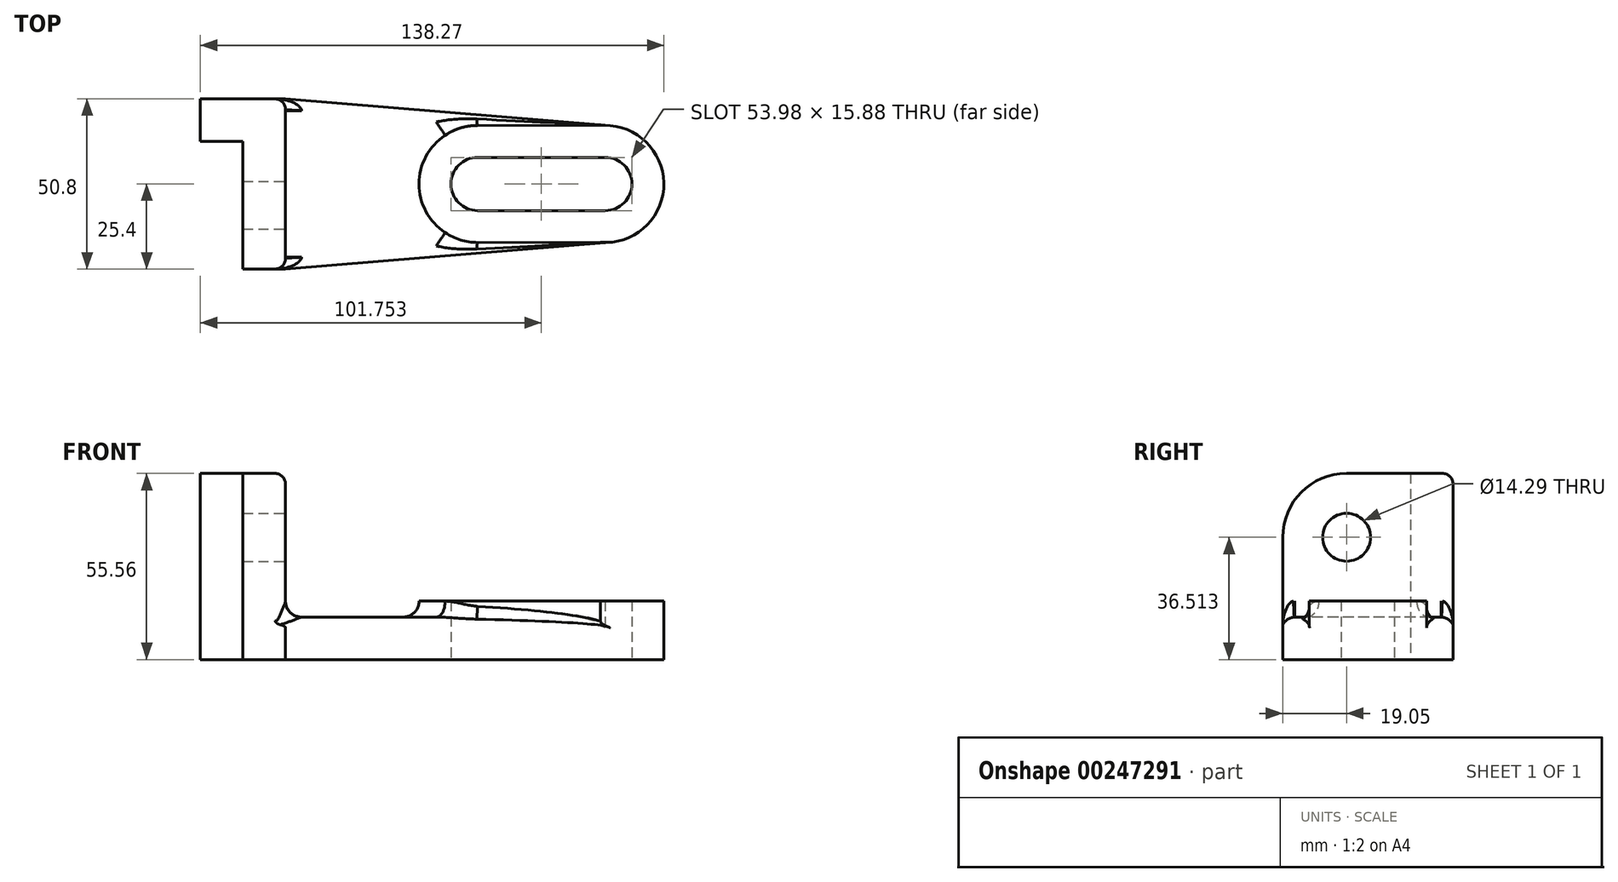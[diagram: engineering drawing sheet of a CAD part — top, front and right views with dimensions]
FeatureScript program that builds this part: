
annotation { "Feature Type Name" : "Feature", "Feature Type Description" : "" }
export const myFeature = defineFeature(function(context is Context, id is Id, definition is map)
    precondition{}
    {
        {
            var Q0;
            Q0=qCreatedBy(makeId("Top.planeOp"),FACE);
            var sketch = newSketch(context, id + "F0", { "sketchPlane" : qUnion([Q0])});
            skLineSegment(sketch, "E0.bottom", {"start": v(-109.54, 25.4) * mm, "end": v(-96.84, 25.4) * mm});
            skLineSegment(sketch, "E0.top", {"start": v(-109.54, -25.4) * mm, "end": v(-96.84, -25.4) * mm});
            skLineSegment(sketch, "E0.left", {"start": v(-109.54, 12.7) * mm, "end": v(-109.54, -25.4) * mm});
            skLineSegment(sketch, "E0.right", {"start": v(-96.84, 25.4) * mm, "end": v(-96.84, -25.4) * mm});
            skLineSegment(sketch, "E1", {"start": v(-109.54, 25.4) * mm, "end": v(-122.24, 25.4) * mm});
            skLineSegment(sketch, "E2", {"start": v(-122.24, 25.4) * mm, "end": v(-122.24, 12.7) * mm});
            skLineSegment(sketch, "E3", {"start": v(-122.24, 12.7) * mm, "end": v(-109.54, 12.7) * mm});
            skLineSegment(sketch, "E4", {"start": v(-96.84, 25.4) * mm, "end": v(0, 17.4) * mm});
            skLineSegment(sketch, "E5", {"start": v(-96.84, -25.4) * mm, "end": v(0, -17.4) * mm});
            skPoint(sketch, "E6", {"position": v(0, 0) * mm});
            skLineSegment(sketch, "E7", {"start": v(-0.02, 17.34) * mm, "end": v(-0.02, 17.34) * mm});
            skLineSegment(sketch, "E8", {"start": v(-0.17, -17.34) * mm, "end": v(-0.17, -17.34) * mm});
            skArc(sketch, "E9", {"start": v(0, -17.4) * mm, "mid": v(16.03, 0) * mm, "end": v(0, 17.4) * mm});
            skSolve(sketch);
        }
        {
            var Q0;
            Q0=makeQuery(id+"F0.imprint","IMPRINT",FACE,{"disambiguationData":[TD([[makeQuery(id+"F0.imprint","IMPRINT",EDGE,{"derivedFrom":sQuery(id+"F0.wireOp",EDGE,"E0.bottom")}),-1.0]])]});
            extrude(context, id + "F1", {"entities" : qUnion([Q0]), "depth" : 55.56 * mm});
        }
        {
            var Q0;
            Q0=makeQuery(id+"F1.opExtrude","CAP_EDGE",EDGE,{"disambiguationData":[OSD([sQuery(id+"F0.wireOp",EDGE,"E0.right")])],"isStart":false});
            var Q1;
            Q1=makeQuery(id+"FIujw7qw0SntBFI_1.boolean.opBoolean","SPLIT",EDGE,{"derivedFrom":makeQuery(id+"F1.opExtrude","SWEPT_EDGE",EDGE,{"disambiguationData":[OSD([sQuery(id+"F0.wireOp",EDGE,"E0.top"),sQuery(id+"F0.wireOp",EDGE,"E0.right"),sQuery(id+"F0.wireOp",EDGE,"E5")])]})});
            var Q2;
            Q2=makeQuery(id+"FIujw7qw0SntBFI_1.boolean.opBoolean","SPLIT",EDGE,{"derivedFrom":makeQuery(id+"F1.opExtrude","SWEPT_EDGE",EDGE,{"disambiguationData":[OSD([sQuery(id+"F0.wireOp",EDGE,"E0.bottom"),sQuery(id+"F0.wireOp",EDGE,"E0.right"),sQuery(id+"F0.wireOp",EDGE,"E4")])]})});
            var Q3;
            Q3=makeQuery(id+"F1.opExtrude","CAP_EDGE",EDGE,{"disambiguationData":[OSD([sQuery(id+"F0.wireOp",EDGE,"E0.bottom"),sQuery(id+"F0.wireOp",EDGE,"E1")])],"isStart":false});
            fillet(context, id + "F2", {"entities" : qUnion([Q0, Q1, Q2, Q3]), "radius" : 3.17 * mm, "tangentPropagation" : true, "allowEdgeOverflow" : false});
        }
        {
            var Q0;
            Q0=makeQuery(id+"F1.opExtrude","CAP_EDGE",EDGE,{"disambiguationData":[OSD([sQuery(id+"F0.wireOp",EDGE,"E0.top")])],"isStart":false});
            fillet(context, id + "F3", {"entities" : qUnion([Q0]), "radius" : 19.05 * mm, "tangentPropagation" : true, "allowEdgeOverflow" : false});
        }
        {
            var Q0;
            Q0 = qSketchRegion(id + "F0", true);
            extrude(context, id + "F4", {"entities" : qUnion([Q0]), "operationType" : NewBodyOperationType.ADD, "depth" : 12.7 * mm});
        }
        {
            var Q0;
            Q0=makeQuery(id+"F4.opExtrude","CAP_FACE",FACE,{"disambiguationData":[OSD([sQuery(id+"F0.wireOp",EDGE,"E0.bottom"),sQuery(id+"F0.wireOp",EDGE,"E0.top"),sQuery(id+"F0.wireOp",EDGE,"E0.left"),sQuery(id+"F0.wireOp",EDGE,"E1"),sQuery(id+"F0.wireOp",EDGE,"E2"),sQuery(id+"F0.wireOp",EDGE,"E3"),sQuery(id+"F0.wireOp",EDGE,"E4"),sQuery(id+"F0.wireOp",EDGE,"E5"),sQuery(id+"F0.wireOp",EDGE,"E9")])],"isStart":false});
            var sketch = newSketch(context, id + "F5", { "sketchPlane" : qUnion([Q0])});
            skArc(sketch, "E10", {"start": v(-2.85, -17.4) * mm, "mid": v(16.01, -0.7) * mm, "end": v(-1.44, 17.46) * mm});
            skArc(sketch, "E11", {"start": v(-1.44, -7.94) * mm, "mid": v(6.5, 0) * mm, "end": v(-1.44, 7.94) * mm});
            skArc(sketch, "E12", {"start": v(-39.54, 17.46) * mm, "mid": v(-57, -0.03) * mm, "end": v(-39.48, -17.46) * mm});
            skArc(sketch, "E13", {"start": v(-39.54, 7.94) * mm, "mid": v(-47.47, 0) * mm, "end": v(-39.54, -7.94) * mm});
            skLineSegment(sketch, "E14", {"start": v(-39.54, 7.94) * mm, "end": v(-1.44, 7.94) * mm});
            skLineSegment(sketch, "E15", {"start": v(-39.54, -7.94) * mm, "end": v(-1.44, -7.94) * mm});
            skLineSegment(sketch, "E16", {"start": v(-1.44, 17.46) * mm, "end": v(-1.44, 17.52) * mm, "construction": true});
            skLineSegment(sketch, "E17", {"start": v(-1.44, 17.52) * mm, "end": v(-1.44, 17.46) * mm, "construction": true});
            skLineSegment(sketch, "E18", {"start": v(-39.54, 17.46) * mm, "end": v(-1.44, 17.52) * mm});
            skLineSegment(sketch, "E19", {"start": v(-39.54, -17.46) * mm, "end": v(-1.44, -17.4) * mm});
            skSolve(sketch);
        }
        {
            var Q0;
            Q0=makeQuery(id+"F5.imprint","IMPRINT",FACE,{"disambiguationData":[TD([[makeQuery(id+"F5.imprint","IMPRINT",EDGE,{"derivedFrom":sQuery(id+"F5.wireOp",EDGE,"E11")}),-1.0]])]});
            extrude(context, id + "F6", {"entities" : qUnion([Q0]), "operationType" : NewBodyOperationType.ADD, "depth" : 4.76 * mm});
        }
        {
            var Q0;
            Q0=makeQuery(id+"F4.opExtrude","CAP_EDGE",EDGE,{"disambiguationData":[OSD([sQuery(id+"F0.wireOp",EDGE,"E5")])],"isStart":false});
            var Q1;
            Q1=makeQuery(id+"F4.opExtrude","CAP_EDGE",EDGE,{"disambiguationData":[OSD([sQuery(id+"F0.wireOp",EDGE,"E4")])],"isStart":false});
            fillet(context, id + "F7", {"entities" : qUnion([Q0, Q1]), "radius" : 3.17 * mm, "tangentPropagation" : true, "allowEdgeOverflow" : false});
        }
        {
            var Q0;
            Q0=makeQuery(id+"F6.opExtrude","CAP_EDGE",EDGE,{"disambiguationData":[OSD([sQuery(id+"F5.wireOp",EDGE,"E12")])],"isStart":true});
            var Q1;
            Q1=makeQuery(id+"F7.opFillet","BLEND_EDGE",EDGE,{"blendedFrom":[makeQuery(id+"F4.opExtrude","CAP_EDGE",EDGE,{"disambiguationData":[OSD([sQuery(id+"F0.wireOp",EDGE,"E5")])],"isStart":false}),makeQuery(id+"F6.opExtrude","SWEPT_FACE",FACE,{"disambiguationData":[OSD([sQuery(id+"F5.wireOp",EDGE,"E19")])]})],"blendedInto":[makeQuery(id+"F6.opExtrude","SWEPT_FACE",FACE,{"disambiguationData":[OSD([sQuery(id+"F5.wireOp",EDGE,"E19")])]})]});
            var Q2;
            Q2=makeQuery(id+"F7.opFillet","BLEND_EDGE",EDGE,{"blendedFrom":[makeQuery(id+"F4.opExtrude","CAP_EDGE",EDGE,{"disambiguationData":[OSD([sQuery(id+"F0.wireOp",EDGE,"E4")])],"isStart":false}),makeQuery(id+"F6.opExtrude","SWEPT_FACE",FACE,{"disambiguationData":[OSD([sQuery(id+"F5.wireOp",EDGE,"E18")])]})],"blendedInto":[makeQuery(id+"F6.opExtrude","SWEPT_FACE",FACE,{"disambiguationData":[OSD([sQuery(id+"F5.wireOp",EDGE,"E18")])]})]});
            fillet(context, id + "F8", {"entities" : qUnion([Q0, Q1, Q2]), "radius" : 4.76 * mm, "tangentPropagation" : true, "allowEdgeOverflow" : false});
        }
        {
            var Q0;
            Q0=makeQuery(id+"F6.boolean.opBoolean","SPLIT",FACE,{"disambiguationData":[TD([makeQuery(id+"F6.opExtrude","SWEPT_FACE",FACE,{"disambiguationData":[OSD([sQuery(id+"F5.wireOp",EDGE,"E11")])]})])],"derivedFrom":makeQuery(id+"F4.opExtrude","CAP_FACE",FACE,{"disambiguationData":[OSD([sQuery(id+"F0.wireOp",EDGE,"E0.bottom"),sQuery(id+"F0.wireOp",EDGE,"E0.top"),sQuery(id+"F0.wireOp",EDGE,"E0.left"),sQuery(id+"F0.wireOp",EDGE,"E1"),sQuery(id+"F0.wireOp",EDGE,"E2"),sQuery(id+"F0.wireOp",EDGE,"E3"),sQuery(id+"F0.wireOp",EDGE,"E4"),sQuery(id+"F0.wireOp",EDGE,"E5"),sQuery(id+"F0.wireOp",EDGE,"E9")])],"isStart":false})});
            extrude(context, id + "F9", {"entities" : qUnion([Q0]), "operationType" : NewBodyOperationType.REMOVE, "endBound" : BoundingType.THROUGH_ALL, "oppositeDirection" : true, "depth" : 25.4 * mm});
        }
        {
            var Q0;
            Q0=makeQuery(id+"F1.opExtrude","SWEPT_FACE",FACE,{"disambiguationData":[OSD([sQuery(id+"F0.wireOp",EDGE,"E0.right")])]});
            var sketch = newSketch(context, id + "F10", { "sketchPlane" : qUnion([Q0])});
            skLineSegment(sketch, "E20", {"start": v(-6.35, 36.51) * mm, "end": v(-22.22, 36.51) * mm, "construction": true});
            skLineSegment(sketch, "E21", {"start": v(-6.35, 52.39) * mm, "end": v(-6.35, 36.51) * mm, "construction": true});
            skCircle(sketch, "E22", {"center": v(-6.35, 36.51) * mm, "radius": 7.14 * mm});
            skSolve(sketch);
        }
        {
            var Q0;
            Q0=makeQuery(id+"F10.imprint","IMPRINT",FACE,{"disambiguationData":[TD([[makeQuery(id+"F10.imprint","IMPRINT",EDGE,{"derivedFrom":sQuery(id+"F10.wireOp",EDGE,"E22")}),1.0]])]});
            extrude(context, id + "F11", {"entities" : qUnion([Q0]), "operationType" : NewBodyOperationType.REMOVE, "endBound" : BoundingType.THROUGH_ALL, "oppositeDirection" : true, "depth" : 25.4 * mm});
        }
        {
            var Q0;
            Q0=makeQuery(id+"F4.boolean.opBoolean","INTERSECT",EDGE,{"derivedFrom":[makeQuery(id+"F1.opExtrude","SWEPT_FACE",FACE,{"disambiguationData":[OSD([sQuery(id+"F0.wireOp",EDGE,"E0.right")])]}),makeQuery(id+"F4.opExtrude","CAP_FACE",FACE,{"disambiguationData":[OSD([sQuery(id+"F0.wireOp",EDGE,"E0.bottom"),sQuery(id+"F0.wireOp",EDGE,"E0.top"),sQuery(id+"F0.wireOp",EDGE,"E0.left"),sQuery(id+"F0.wireOp",EDGE,"E1"),sQuery(id+"F0.wireOp",EDGE,"E2"),sQuery(id+"F0.wireOp",EDGE,"E3"),sQuery(id+"F0.wireOp",EDGE,"E4"),sQuery(id+"F0.wireOp",EDGE,"E5"),sQuery(id+"F0.wireOp",EDGE,"E9")])],"isStart":false})]});
            fillet(context, id + "F12", {"entities" : qUnion([Q0]), "radius" : 4.76 * mm, "tangentPropagation" : true, "allowEdgeOverflow" : false});
        }
    });
